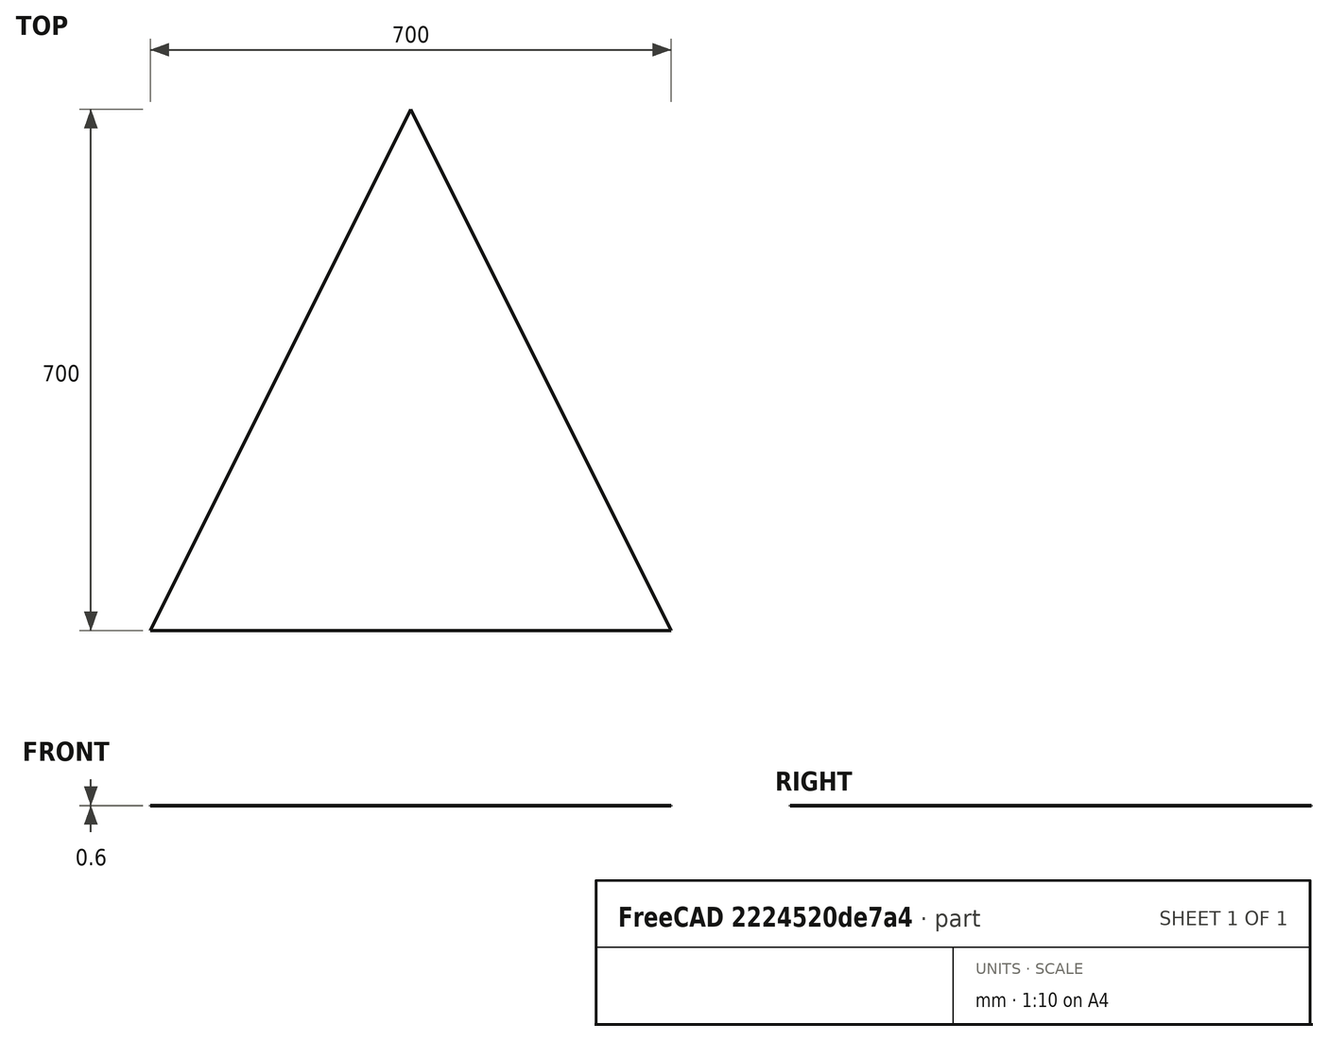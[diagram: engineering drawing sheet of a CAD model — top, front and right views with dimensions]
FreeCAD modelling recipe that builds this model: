
FCSTD DOCUMENT  (FreeCAD 0.18R4 (GitTag))
Label: body
License: All rights reserved
LicenseURL: http://en.wikipedia.org/wiki/All_rights_reserved
objects: Sketcher::SketchObject×1, PartDesign::Pad×1, PartDesign::Body×1
note: 4 computed .brp shape members not serialized (recipe doc carries the construction recipe); baked Part::Feature solids carry a one-line shape summary decoded from their .brp

FEATURE [Sketcher::SketchObject] Sketch
  MapMode = 5
  Support = -> [XY_Plane]
  sketch-geometry (4):
    g0: LineSegment StartX=-350 StartY=0 StartZ=0 EndX=0 EndY=700 EndZ=0
    g1: LineSegment StartX=4.9e-15 StartY=700 StartZ=0 EndX=350 EndY=0 EndZ=0
    g2: LineSegment StartX=350 StartY=0 StartZ=0 EndX=0 EndY=0 EndZ=0
    g3: LineSegment StartX=-350 StartY=0 StartZ=0 EndX=0 EndY=0 EndZ=0
  constraints (11):
    c: Horizontal(g2)
    c: Horizontal(g3)
    c: Equal(g0,g1)
    c: Coincident(g0,g3)
    c: Coincident(g3,g-1)
    c: Equal(g3,g2)
    c: Coincident(g0,g1)
    c: Coincident(g1,g2)
    c: Coincident(g2,g3)
    c: DistanceY(g2,g0) = 700
    c: DistanceX(g0,g1) = 700
FEATURE [PartDesign::Pad] Pad
  Length = 0.6
  Length2 = 100
  Profile = -> Sketch
  Type = 0
FEATURE [PartDesign::Body] Body
  Group = -> [Sketch,Pad]
  Origin = -> Origin
  Tip = -> Pad
